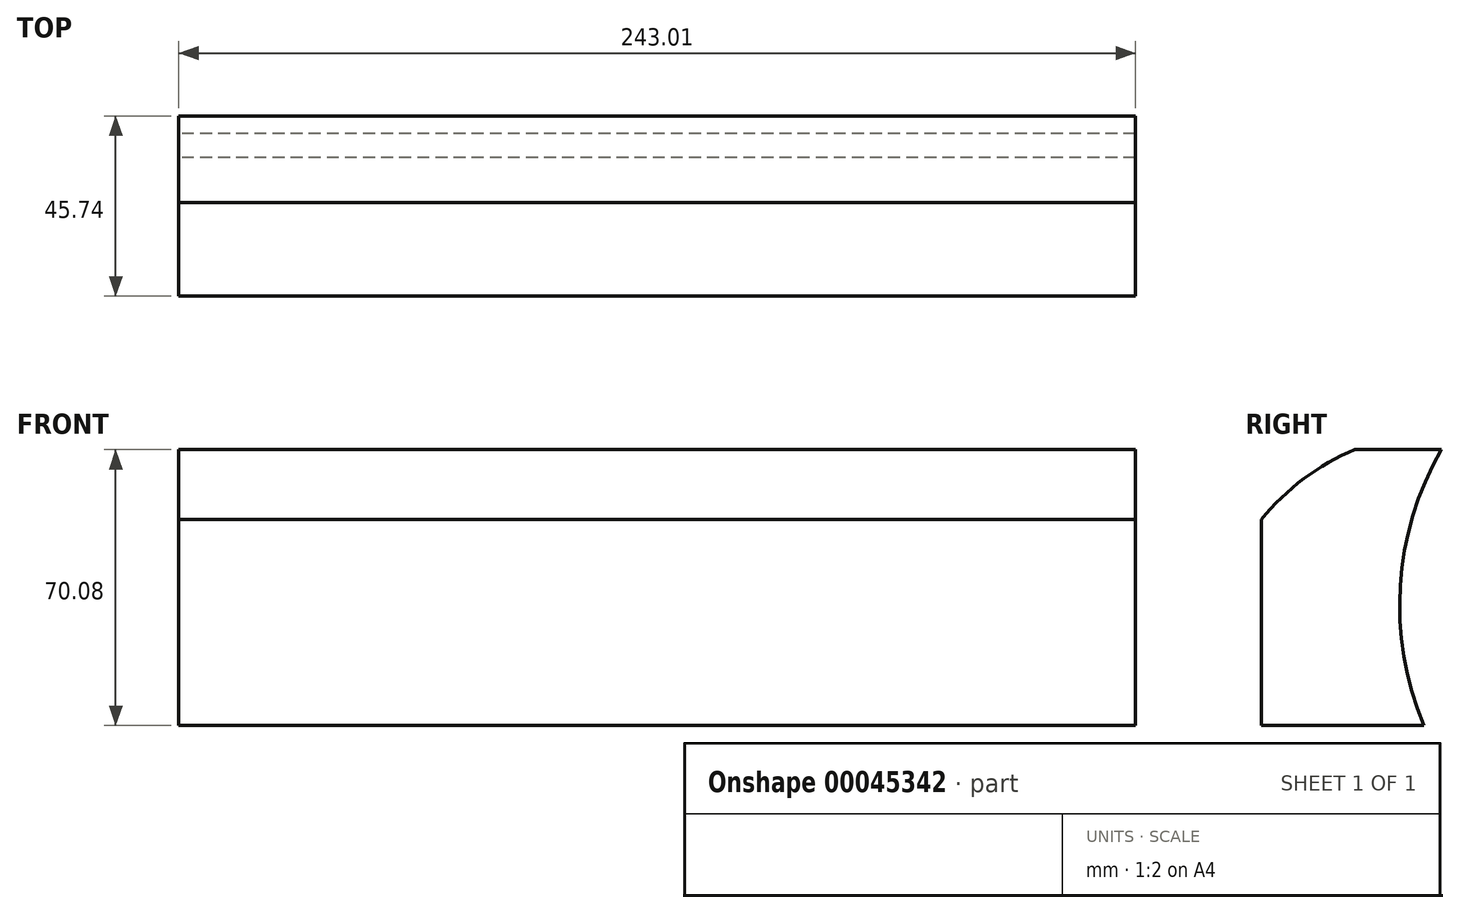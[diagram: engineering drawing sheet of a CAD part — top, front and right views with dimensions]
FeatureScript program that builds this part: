
annotation { "Feature Type Name" : "Feature", "Feature Type Description" : "" }
export const myFeature = defineFeature(function(context is Context, id is Id, definition is map)
    precondition{}
    {
        {
            var Q0;
            Q0=qCreatedBy(makeId("Right.planeOp"),FACE);
            var sketch = newSketch(context, id + "F0", { "sketchPlane" : qUnion([Q0])});
            skLineSegment(sketch, "E0.rect.bottom", {"start": v(18.07, -57.9) * mm, "end": v(87.16, -57.9) * mm});
            skLineSegment(sketch, "E0.rect.top", {"start": v(18.07, 12.17) * mm, "end": v(87.16, 12.17) * mm});
            skLineSegment(sketch, "E0.rect.left", {"start": v(18.07, -57.9) * mm, "end": v(18.07, 12.17) * mm});
            skLineSegment(sketch, "E0.rect.right", {"start": v(87.16, -57.9) * mm, "end": v(87.16, 12.17) * mm});
            skPoint(sketch, "E0.rect.middle", {"position": v(52.61, -22.87) * mm});
            skArc(sketch, "E1", {"start": v(118.98, -18.8) * mm, "mid": v(5.14, -47.8) * mm, "end": v(122.18, -57.9) * mm});
            skArc(sketch, "E2", {"start": v(176.14, 38.81) * mm, "mid": v(53.76, -18.2) * mm, "end": v(159.7, -101.9) * mm});
            skArc(sketch, "E3", {"start": v(23.56, -41.23) * mm, "mid": v(64.17, -172.89) * mm, "end": v(138.63, -288.81) * mm});
            skSolve(sketch);
        }
        {
            var Q0;
            {var subQ3=sQuery(id+"F0.wireOp",EDGE,"E0.rect.bottom");var subQ6=sQuery(id+"F0.wireOp",EDGE,"E0.rect.left");var subQ10=makeQuery(id+"F0.imprint","INTERSECT",VERTEX,{"derivedFrom":[subQ3,subQ6]});Q0=makeQuery(id+"F0.imprint","IMPRINT",FACE,{"disambiguationData":[TD([[makeQuery(id+"F0.imprint","IMPRINT",EDGE,{"disambiguationData":[TD([[subQ10,-1.0]])],"derivedFrom":subQ3}),1.0]])]});}
            extrude(context, id + "F1", {"entities" : qUnion([Q0]), "depth" : 243 * mm});
        }
    });
